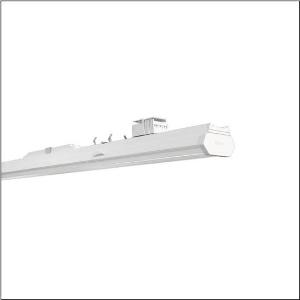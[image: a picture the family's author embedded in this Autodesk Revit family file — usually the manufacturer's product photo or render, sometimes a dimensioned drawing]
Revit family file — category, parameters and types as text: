
# Revit family: licross_11_protected_mo_51tp11mn495g
name_source: partatom
category: Lighting Fixtures
units: mm (PartAtom-declared; Revit-internal decimal feet)

## family parameters
Cut with Voids When Loaded = No
Host = Face
Light Source = No
Part Type = Normal
Room Calculation Point = No
Round Connector Dimension = Use Diameter
Shared = No

## types (1)
- --- (1 x LED, 9980 lm, 55.3 W, 4000K)
    Apparent Load = 55 VA
    CIE Flux Codes = 83 94 98 100 100
    Color Rendering = 80
    Color Temperature = 4000K
    Default Elevation = 1800 mm
    Description = Licross 11 Protected MO, luminaire insert, of sheet steel, galvanised, coil coated, white, length: 1.500mm, width: 90mm, height: 101mm, LED rated luminous flux: 9.980lm, light colour: 840, SDCM (Standard Deviation of Colour Matching)MacAdam ≤ 2 SDCM (initial), control gear: ON/OFF Multilumen, with plug, 3-pole, with phase selection, mains connection: 220..240V, AC, 50/60Hz, rated input power: 55W, internal wiring halogen-free, primary light control with lens, of plastic, primary optical cover: cover, of PMMA, light emission: direct distribution, primary light characteristic: symmetric, protection rating (complete): IP64, insulation class (complete): insulation class I (protective earthing), certification: CE, ENEC, VDE, UKCA, protection symbol: D if used in an environment with conductive dust loads with corresponding accessories, impact resistance: IK06, permissible ambient temperature for indoor applications: -35..+40°C, corresponds to IFS (International Featured Standards) requirements for safety and quality in the food industry, reducing of maximum allowable ambient temperature of 5°C with ceiling mounting, LABS conformity tested according to VDMA 24364:2018-05, The light source and the operating device comply with the requirements of the Ecodesign Regulation (EU) 2019/2020 and are replaceable in accordance with this regulation, packaging unit: 1 piece
    Height = 92 mm
    Lamp = 1 x LED
    Lamp Light Flux = 9980 lm
    Lamp Power = 55.3 W
    Lamp count = 1
    Length = 1500 mm
    Luminous efficacy = 180 lm/W
    Manufacturer = Siteco
    ModVariant = No
    Model = 51TP11MN495G
    Mounting Place = Ceiling
    Mounting Type = Pendant
    Number of Poles = 1
    OnlyDefault = Yes
    Power Factor = 1
    Product Name = Licross 11 Protected MO
    Product group = luminaire insert | ceiling pendant
    ProductGroupID = 901
    Protection Class = Protection class I
    Protection Degree = IP 64
    RLX_Detail_Level = 1
    RLX_Emergency_Light_Flux = 0 lm
    RLX_Emergency_Type = 0
    RLX_Emergency_Type_DB = No
    RlxData = <blob elided: 22181 chars, md5=8cd2d3b3>
    Socket = socket
    Standby Power = 0 W
    System Light Flux = 9980 lm
    System Power = 55 W
    Type Comments = factory setting: luminous flux: 100 % | (A | C | E) | 126 mA
    Type Image = l_1256148.jpg
    URL = http://relux.com
    VarID = @adj_091943
    Voltage = 0 V
    Weight = 0.00 kg
    Width = 88 mm

## geometry (parser evidence)
native form markers: Blend x4, Sweep x10
no freeform markers — native parametric forms only
